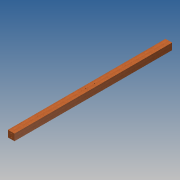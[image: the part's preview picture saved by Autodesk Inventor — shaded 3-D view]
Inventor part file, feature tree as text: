
AUTODESK INVENTOR PART (.ipt)
format: ipt  version: 2014 SP1 (Build 180222100, 222)  size: 104,448 bytes
history: native  units: in
note: dims shown in document units (in); Inventor stores cm internally (conversion verified against a paired STEP export)
features: sketch x4, hole x3, extrude x1
ambient origin geometry x8: Origin, YZ Plane, XZ Plane, XY Plane, X Axis, Y Axis, Z Axis, Center Point
bodies: Solid1 (feature_tree)
feature tree (8):
  extrude  "Extrusion1"  Depth=1.5in
  hole  "Hole4"  [1 undecoded]
  hole  "Hole5"  [1 undecoded]
  hole  "Hole6"  [1 undecoded]
  sketch  "Sketch1"  dims[d0=1.5in d1=1.5in]
  sketch  "Sketch5"  dims[d2=36.0in d3=0.0in d51=1.0in]
  sketch  "Sketch6"  dims[d52=0.201in d53=0.75in d54=0.385in d55=0.25in d56=0.5635in d57=1.0in d58=0.8108in d59=0.375in]
  sketch  "Sketch7"  dims[d60=0.201in d61=0.75in d62=0.385in d63=0.25in d64=0.5635in d65=1.0in d66=0.8108in d67=0.375in d68=0.201in d69=0.75in d70=0.385in d71=0.25in d72=0.5635in d73=1.0in d74=0.8108in]
note: 3 required parameter values undecoded (feature->parameter linkage not recoverable at this tier; creation-order binding heuristic only, values carry confidence <= 0.55)
